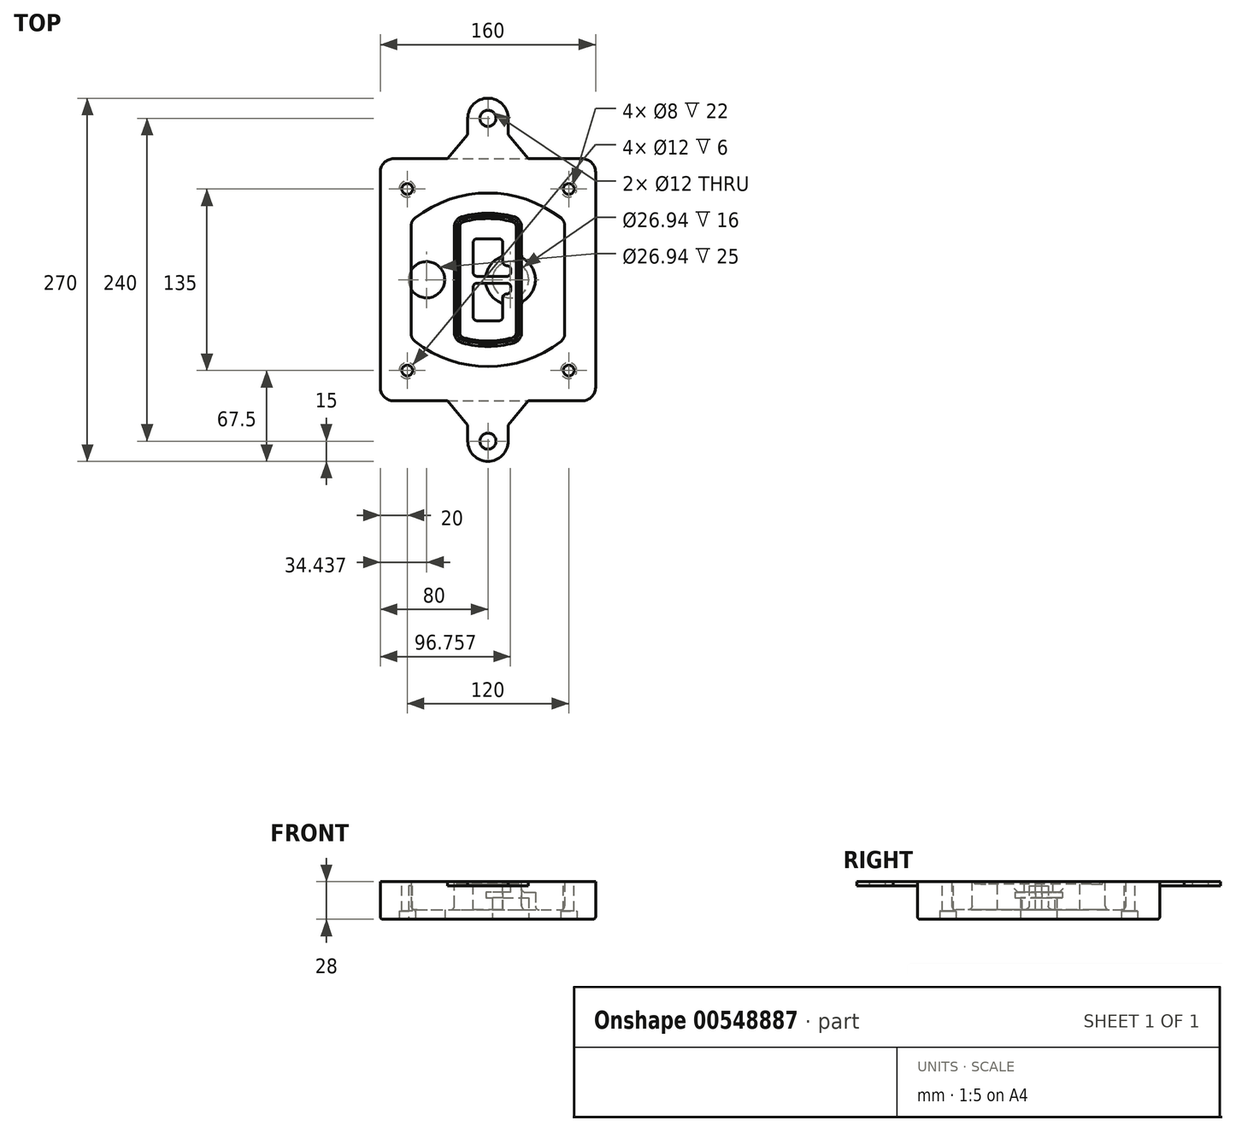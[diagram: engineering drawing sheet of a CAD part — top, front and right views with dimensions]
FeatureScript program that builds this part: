
annotation { "Feature Type Name" : "Feature", "Feature Type Description" : "" }
export const myFeature = defineFeature(function(context is Context, id is Id, definition is map)
    precondition{}
    {
        {
            var Q0;
            Q0=qCreatedBy(makeId("Top.planeOp"),FACE);
            var sketch = newSketch(context, id + "F0", { "sketchPlane" : qUnion([Q0])});
            skPoint(sketch, "E0.rect.middle", {"position": v(0, 0) * mm});
            skLineSegment(sketch, "E1.bottom", {"start": v(-70, -90) * mm, "end": v(70, -90) * mm});
            skLineSegment(sketch, "E1.top", {"start": v(-70, 90) * mm, "end": v(70, 90) * mm});
            skLineSegment(sketch, "E1.left", {"start": v(-80, -80) * mm, "end": v(-80, 80) * mm});
            skLineSegment(sketch, "E1.right", {"start": v(80, -80) * mm, "end": v(80, 80) * mm});
            skLineSegment(sketch, "E2", {"start": v(-80, 90) * mm, "end": v(80, -90) * mm, "construction": true});
            skLineSegment(sketch, "E3", {"start": v(80, 90) * mm, "end": v(-80, -90) * mm, "construction": true});
            skCircle(sketch, "E4", {"center": v(-60, 67.5) * mm, "radius": 4 * mm});
            skCircle(sketch, "E5", {"center": v(60, 67.5) * mm, "radius": 4 * mm});
            skCircle(sketch, "E6", {"center": v(60, -67.5) * mm, "radius": 4 * mm});
            skCircle(sketch, "E7", {"center": v(-60, -67.5) * mm, "radius": 4 * mm});
            skLineSegment(sketch, "E8", {"start": v(-60, 67.5) * mm, "end": v(60, 67.5) * mm, "construction": true});
            skLineSegment(sketch, "E9", {"start": v(60, 67.5) * mm, "end": v(60, -67.5) * mm, "construction": true});
            skLineSegment(sketch, "E10", {"start": v(60, -67.5) * mm, "end": v(-60, -67.5) * mm, "construction": true});
            skLineSegment(sketch, "E11", {"start": v(-60, -67.5) * mm, "end": v(-60, 67.5) * mm, "construction": true});
            skLineSegment(sketch, "E12", {"start": v(-60, 40.3) * mm, "end": v(-60, -40.3) * mm});
            skLineSegment(sketch, "E13", {"start": v(60, 40.3) * mm, "end": v(60, -40.3) * mm});
            skArc(sketch, "E14", {"start": v(56.15, 48.18) * mm, "mid": v(0, 67.5) * mm, "end": v(-56.15, 48.18) * mm});
            skArc(sketch, "E15", {"start": v(-56.15, -48.18) * mm, "mid": v(0, -67.5) * mm, "end": v(56.15, -48.18) * mm});
            skLineSegment(sketch, "E16", {"start": v(-60, 0) * mm, "end": v(60, 0) * mm, "construction": true});
            skPoint(sketch, "E17.visualSharp", {"position": v(-60, -45) * mm});
            skArc(sketch, "E17.filletArc", {"start": v(-60, -40.3) * mm, "mid": v(-58.99, -44.68) * mm, "end": v(-56.15, -48.18) * mm});
            skPoint(sketch, "E18.visualSharp", {"position": v(-60, 45) * mm});
            skArc(sketch, "E18.filletArc", {"start": v(-56.15, 48.18) * mm, "mid": v(-58.99, 44.68) * mm, "end": v(-60, 40.3) * mm});
            skPoint(sketch, "E19.visualSharp", {"position": v(60, 45) * mm});
            skArc(sketch, "E19.filletArc", {"start": v(60, 40.3) * mm, "mid": v(58.99, 44.68) * mm, "end": v(56.15, 48.18) * mm});
            skPoint(sketch, "E20.visualSharp", {"position": v(60, -45) * mm});
            skArc(sketch, "E20.filletArc", {"start": v(56.15, -48.18) * mm, "mid": v(58.99, -44.68) * mm, "end": v(60, -40.3) * mm});
            skPoint(sketch, "E21.visualSharp", {"position": v(-80, 90) * mm});
            skArc(sketch, "E21.filletArc", {"start": v(-70, 90) * mm, "mid": v(-77.07, 87.07) * mm, "end": v(-80, 80) * mm});
            skPoint(sketch, "E22.visualSharp", {"position": v(80, 90) * mm});
            skArc(sketch, "E22.filletArc", {"start": v(80, 80) * mm, "mid": v(77.07, 87.07) * mm, "end": v(70, 90) * mm});
            skPoint(sketch, "E23.visualSharp", {"position": v(80, -90) * mm});
            skArc(sketch, "E23.filletArc", {"start": v(70, -90) * mm, "mid": v(77.07, -87.07) * mm, "end": v(80, -80) * mm});
            skPoint(sketch, "E24.visualSharp", {"position": v(-80, -90) * mm});
            skArc(sketch, "E24.filletArc", {"start": v(-80, -80) * mm, "mid": v(-77.07, -87.07) * mm, "end": v(-70, -90) * mm});
            skArc(sketch, "E25.0", {"start": v(57, 40.3) * mm, "mid": v(56.3, 43.36) * mm, "end": v(54.3, 45.81) * mm});
            skLineSegment(sketch, "E25.1", {"start": v(57, 40.3) * mm, "end": v(57, -40.3) * mm});
            skArc(sketch, "E25.2", {"start": v(54.3, -45.81) * mm, "mid": v(56.3, -43.36) * mm, "end": v(57, -40.3) * mm});
            skArc(sketch, "E25.3", {"start": v(-54.3, -45.81) * mm, "mid": v(0, -64.5) * mm, "end": v(54.3, -45.81) * mm});
            skArc(sketch, "E25.4", {"start": v(-57, -40.3) * mm, "mid": v(-56.3, -43.36) * mm, "end": v(-54.3, -45.81) * mm});
            skArc(sketch, "E25.5", {"start": v(54.3, 45.81) * mm, "mid": v(0, 64.5) * mm, "end": v(-54.3, 45.81) * mm});
            skLineSegment(sketch, "E25.6", {"start": v(-57, 40.3) * mm, "end": v(-57, -40.3) * mm});
            skArc(sketch, "E25.7", {"start": v(-54.3, 45.81) * mm, "mid": v(-56.3, 43.36) * mm, "end": v(-57, 40.3) * mm});
            skArc(sketch, "E26.0", {"start": v(-58.62, 51.33) * mm, "mid": v(-62.58, 46.43) * mm, "end": v(-64, 40.3) * mm});
            skArc(sketch, "E26.1", {"start": v(58.62, 51.33) * mm, "mid": v(0, 71.5) * mm, "end": v(-58.62, 51.33) * mm});
            skArc(sketch, "E26.2", {"start": v(64, 40.3) * mm, "mid": v(62.58, 46.43) * mm, "end": v(58.62, 51.33) * mm});
            skLineSegment(sketch, "E26.3", {"start": v(64, 40.3) * mm, "end": v(64, -40.3) * mm});
            skArc(sketch, "E26.4", {"start": v(58.62, -51.33) * mm, "mid": v(62.58, -46.43) * mm, "end": v(64, -40.3) * mm});
            skLineSegment(sketch, "E26.5", {"start": v(-64, 40.3) * mm, "end": v(-64, -40.3) * mm});
            skArc(sketch, "E26.6", {"start": v(-58.62, -51.33) * mm, "mid": v(0, -71.5) * mm, "end": v(58.62, -51.33) * mm});
            skArc(sketch, "E26.7", {"start": v(-64, -40.3) * mm, "mid": v(-62.58, -46.43) * mm, "end": v(-58.62, -51.33) * mm});
            skSolve(sketch);
        }
        {
            var Q0;
            Q0=makeQuery(id+"F0.imprint","IMPRINT",FACE,{"disambiguationData":[TD([[makeQuery(id+"F0.imprint","IMPRINT",EDGE,{"derivedFrom":sQuery(id+"F0.wireOp",EDGE,"E1.bottom")}),1.0]])]});
            var Q1;
            Q1=makeQuery(id+"F0.imprint","IMPRINT",FACE,{"disambiguationData":[TD([[makeQuery(id+"F0.imprint","IMPRINT",EDGE,{"derivedFrom":sQuery(id+"F0.wireOp",EDGE,"E12")}),1.0]])]});
            var Q2;
            Q2=makeQuery(id+"F0.imprint","IMPRINT",FACE,{"disambiguationData":[TD([[makeQuery(id+"F0.imprint","IMPRINT",EDGE,{"derivedFrom":sQuery(id+"F0.wireOp",EDGE,"E25.0")}),1.0]])]});
            var Q3;
            Q3=makeQuery(id+"F0.imprint","IMPRINT",FACE,{"disambiguationData":[TD([[makeQuery(id+"F0.imprint","IMPRINT",EDGE,{"derivedFrom":sQuery(id+"F0.wireOp",EDGE,"E12")}),-1.0]])]});
            extrude(context, id + "F1", {"entities" : qUnion([Q0, Q1, Q2, Q3]), "oppositeDirection" : true, "depth" : 25 * mm, "offsetDistance" : 25 * mm});
        }
        {
            var Q0;
            Q0=makeQuery(id+"F0.imprint","IMPRINT",FACE,{"disambiguationData":[TD([[makeQuery(id+"F0.imprint","IMPRINT",EDGE,{"derivedFrom":sQuery(id+"F0.wireOp",EDGE,"E12")}),1.0]])]});
            extrude(context, id + "F2", {"entities" : qUnion([Q0]), "operationType" : NewBodyOperationType.ADD, "depth" : 3 * mm});
        }
        {
            var Q0;
            Q0=makeQuery(id+"F0.imprint","IMPRINT",FACE,{"disambiguationData":[TD([[makeQuery(id+"F0.imprint","IMPRINT",EDGE,{"derivedFrom":sQuery(id+"F0.wireOp",EDGE,"E25.0")}),1.0]])]});
            extrude(context, id + "F3", {"entities" : qUnion([Q0]), "operationType" : NewBodyOperationType.REMOVE, "oppositeDirection" : true, "depth" : 18 * mm});
        }
        {
            var Q0;
            Q0=makeQuery(id+"F2.opExtrude","CAP_FACE",FACE,{"disambiguationData":[OSD([sQuery(id+"F0.wireOp",EDGE,"E12"),sQuery(id+"F0.wireOp",EDGE,"E13"),sQuery(id+"F0.wireOp",EDGE,"E14"),sQuery(id+"F0.wireOp",EDGE,"E15"),sQuery(id+"F0.wireOp",EDGE,"E17.filletArc"),sQuery(id+"F0.wireOp",EDGE,"E18.filletArc"),sQuery(id+"F0.wireOp",EDGE,"E19.filletArc"),sQuery(id+"F0.wireOp",EDGE,"E20.filletArc"),sQuery(id+"F0.wireOp",EDGE,"E25.0"),sQuery(id+"F0.wireOp",EDGE,"E25.1"),sQuery(id+"F0.wireOp",EDGE,"E25.2"),sQuery(id+"F0.wireOp",EDGE,"E25.3"),sQuery(id+"F0.wireOp",EDGE,"E25.4"),sQuery(id+"F0.wireOp",EDGE,"E25.5"),sQuery(id+"F0.wireOp",EDGE,"E25.6"),sQuery(id+"F0.wireOp",EDGE,"E25.7")])],"isStart":false});
            var sketch = newSketch(context, id + "F4", { "sketchPlane" : qUnion([Q0])});
            skArc(sketch, "E27.0", {"start": v(-19.08, -46.97) * mm, "mid": v(0, -49.5) * mm, "end": v(19.08, -46.97) * mm});
            skArc(sketch, "E28.0", {"start": v(19.08, 46.97) * mm, "mid": v(0, 49.5) * mm, "end": v(-19.08, 46.97) * mm});
            skLineSegment(sketch, "E29", {"start": v(-25, 39.25) * mm, "end": v(-25, -39.25) * mm});
            skLineSegment(sketch, "E30", {"start": v(25, 39.25) * mm, "end": v(25, -39.25) * mm});
            skLineSegment(sketch, "E31", {"start": v(-25, 45.1) * mm, "end": v(25, 45.1) * mm, "construction": true});
            skLineSegment(sketch, "E32", {"start": v(-25, -45.1) * mm, "end": v(25, -45.1) * mm, "construction": true});
            skPoint(sketch, "E33.visualSharp", {"position": v(-25, 45.1) * mm});
            skArc(sketch, "E33.filletArc", {"start": v(-19.08, 46.97) * mm, "mid": v(-23.35, 44.11) * mm, "end": v(-25, 39.25) * mm});
            skPoint(sketch, "E34.visualSharp", {"position": v(25, 45.1) * mm});
            skArc(sketch, "E34.filletArc", {"start": v(25, 39.25) * mm, "mid": v(23.35, 44.11) * mm, "end": v(19.08, 46.97) * mm});
            skPoint(sketch, "E35.visualSharp", {"position": v(25, -45.1) * mm});
            skArc(sketch, "E35.filletArc", {"start": v(19.08, -46.97) * mm, "mid": v(23.35, -44.11) * mm, "end": v(25, -39.25) * mm});
            skPoint(sketch, "E36.visualSharp", {"position": v(-25, -45.1) * mm});
            skArc(sketch, "E36.filletArc", {"start": v(-25, -39.25) * mm, "mid": v(-23.35, -44.11) * mm, "end": v(-19.08, -46.97) * mm});
            skArc(sketch, "E37.0", {"start": v(54.3, 45.81) * mm, "mid": v(0, 64.5) * mm, "end": v(-54.3, 45.81) * mm});
            skArc(sketch, "E37.1", {"start": v(-54.3, 45.81) * mm, "mid": v(-56.3, 43.36) * mm, "end": v(-57, 40.3) * mm});
            skLineSegment(sketch, "E37.2", {"start": v(-57, 40.3) * mm, "end": v(-57, -40.3) * mm});
            skArc(sketch, "E37.3", {"start": v(-57, -40.3) * mm, "mid": v(-56.3, -43.36) * mm, "end": v(-54.3, -45.81) * mm});
            skArc(sketch, "E37.4", {"start": v(-54.3, -45.81) * mm, "mid": v(0, -64.5) * mm, "end": v(54.3, -45.81) * mm});
            skArc(sketch, "E37.5", {"start": v(54.3, -45.81) * mm, "mid": v(56.3, -43.36) * mm, "end": v(57, -40.3) * mm});
            skLineSegment(sketch, "E37.6", {"start": v(57, 40.3) * mm, "end": v(57, -40.3) * mm});
            skArc(sketch, "E37.7", {"start": v(57, 40.3) * mm, "mid": v(56.3, 43.36) * mm, "end": v(54.3, 45.81) * mm});
            skLineSegment(sketch, "E38.0", {"start": v(23, 39.25) * mm, "end": v(23, -39.25) * mm});
            skArc(sketch, "E38.1", {"start": v(18.56, -45.04) * mm, "mid": v(21.76, -42.9) * mm, "end": v(23, -39.25) * mm});
            skArc(sketch, "E38.2", {"start": v(-18.56, -45.04) * mm, "mid": v(0, -47.5) * mm, "end": v(18.56, -45.04) * mm});
            skArc(sketch, "E38.3", {"start": v(-23, -39.25) * mm, "mid": v(-21.76, -42.9) * mm, "end": v(-18.56, -45.04) * mm});
            skLineSegment(sketch, "E38.4", {"start": v(-23, 39.25) * mm, "end": v(-23, -39.25) * mm});
            skArc(sketch, "E38.5", {"start": v(23, 39.25) * mm, "mid": v(21.76, 42.9) * mm, "end": v(18.56, 45.04) * mm});
            skArc(sketch, "E38.6", {"start": v(-18.56, 45.04) * mm, "mid": v(-21.76, 42.9) * mm, "end": v(-23, 39.25) * mm});
            skArc(sketch, "E38.7", {"start": v(18.56, 45.04) * mm, "mid": v(0, 47.5) * mm, "end": v(-18.56, 45.04) * mm});
            skArc(sketch, "E39.0", {"start": v(21, 39.25) * mm, "mid": v(20.18, 41.68) * mm, "end": v(18.04, 43.1) * mm});
            skLineSegment(sketch, "E39.1", {"start": v(21, 39.25) * mm, "end": v(21, -39.25) * mm});
            skArc(sketch, "E39.2", {"start": v(18.04, -43.1) * mm, "mid": v(20.18, -41.68) * mm, "end": v(21, -39.25) * mm});
            skArc(sketch, "E39.3", {"start": v(-18.04, -43.1) * mm, "mid": v(0, -45.5) * mm, "end": v(18.04, -43.1) * mm});
            skArc(sketch, "E39.4", {"start": v(-21, -39.25) * mm, "mid": v(-20.18, -41.68) * mm, "end": v(-18.04, -43.1) * mm});
            skArc(sketch, "E39.5", {"start": v(18.04, 43.1) * mm, "mid": v(0, 45.5) * mm, "end": v(-18.04, 43.1) * mm});
            skLineSegment(sketch, "E39.6", {"start": v(-21, 39.25) * mm, "end": v(-21, -39.25) * mm});
            skArc(sketch, "E39.7", {"start": v(-18.04, 43.1) * mm, "mid": v(-20.18, 41.68) * mm, "end": v(-21, 39.25) * mm});
            skLineSegment(sketch, "E40", {"start": v(-25, 0) * mm, "end": v(25, 0) * mm, "construction": true});
            skLineSegment(sketch, "E41", {"start": v(-11, 5.5) * mm, "end": v(-11, 27.5) * mm});
            skLineSegment(sketch, "E42", {"start": v(-8, 30.5) * mm, "end": v(8, 30.5) * mm});
            skLineSegment(sketch, "E43", {"start": v(11, 27.5) * mm, "end": v(11, 13.5) * mm});
            skLineSegment(sketch, "E44", {"start": v(14, 10.5) * mm, "end": v(14, 10.5) * mm});
            skLineSegment(sketch, "E45", {"start": v(17, 7.5) * mm, "end": v(17, 5.5) * mm});
            skLineSegment(sketch, "E46", {"start": v(14, 2.5) * mm, "end": v(-8, 2.5) * mm});
            skPoint(sketch, "E47.visualSharp", {"position": v(-11, 30.5) * mm});
            skArc(sketch, "E47.filletArc", {"start": v(-8, 30.5) * mm, "mid": v(-10.12, 29.62) * mm, "end": v(-11, 27.5) * mm});
            skPoint(sketch, "E48.visualSharp", {"position": v(11, 30.5) * mm});
            skArc(sketch, "E48.filletArc", {"start": v(11, 27.5) * mm, "mid": v(10.12, 29.62) * mm, "end": v(8, 30.5) * mm});
            skPoint(sketch, "E49.visualSharp", {"position": v(11, 10.5) * mm});
            skArc(sketch, "E49.filletArc", {"start": v(11, 13.5) * mm, "mid": v(11.88, 11.38) * mm, "end": v(14, 10.5) * mm});
            skPoint(sketch, "E50.visualSharp", {"position": v(17, 10.5) * mm});
            skArc(sketch, "E50.filletArc", {"start": v(17, 7.5) * mm, "mid": v(16.12, 9.62) * mm, "end": v(14, 10.5) * mm});
            skPoint(sketch, "E51.visualSharp", {"position": v(17, 2.5) * mm});
            skArc(sketch, "E51.filletArc", {"start": v(14, 2.5) * mm, "mid": v(16.12, 3.38) * mm, "end": v(17, 5.5) * mm});
            skPoint(sketch, "E52.visualSharp", {"position": v(-11, 2.5) * mm});
            skArc(sketch, "E52.filletArc", {"start": v(-11, 5.5) * mm, "mid": v(-10.12, 3.38) * mm, "end": v(-8, 2.5) * mm});
            skLineSegment(sketch, "E53.0.MirrorCS", {"start": v(14, -2.5) * mm, "end": v(-8, -2.5) * mm});
            skArc(sketch, "E54.0.MirrorCS", {"start": v(-11, -5.5) * mm, "mid": v(-10.12, -3.38) * mm, "end": v(-8, -2.5) * mm});
            skLineSegment(sketch, "E55.0.MirrorCS", {"start": v(-11, -5.5) * mm, "end": v(-11, -27.5) * mm});
            skArc(sketch, "E56.0.MirrorCS", {"start": v(-8, -30.5) * mm, "mid": v(-10.12, -29.62) * mm, "end": v(-11, -27.5) * mm});
            skLineSegment(sketch, "E57.0.MirrorCS", {"start": v(-8, -30.5) * mm, "end": v(8, -30.5) * mm});
            skArc(sketch, "E58.0.MirrorCS", {"start": v(11, -27.5) * mm, "mid": v(10.12, -29.62) * mm, "end": v(8, -30.5) * mm});
            skLineSegment(sketch, "E59.0.MirrorCS", {"start": v(11, -27.5) * mm, "end": v(11, -13.5) * mm});
            skArc(sketch, "E60.0.MirrorCS", {"start": v(11, -13.5) * mm, "mid": v(11.88, -11.38) * mm, "end": v(14, -10.5) * mm});
            skArc(sketch, "E61.0.MirrorCS", {"start": v(17, -7.5) * mm, "mid": v(16.12, -9.62) * mm, "end": v(14, -10.5) * mm});
            skLineSegment(sketch, "E62.0.MirrorCS", {"start": v(17, -7.5) * mm, "end": v(17, -5.5) * mm});
            skArc(sketch, "E63.0.MirrorCS", {"start": v(14, -2.5) * mm, "mid": v(16.12, -3.38) * mm, "end": v(17, -5.5) * mm});
            skSolve(sketch);
        }
        {
            var Q0;
            Q0=makeQuery(id+"F4.imprint","IMPRINT",FACE,{"disambiguationData":[TD([[makeQuery(id+"F4.imprint","IMPRINT",EDGE,{"derivedFrom":sQuery(id+"F4.wireOp",EDGE,"E27.0")}),1.0]])]});
            var Q1;
            Q1=makeQuery(id+"F4.imprint","IMPRINT",FACE,{"disambiguationData":[TD([[makeQuery(id+"F4.imprint","IMPRINT",EDGE,{"derivedFrom":sQuery(id+"F4.wireOp",EDGE,"E38.0")}),-1.0]])]});
            var Q2;
            Q2=makeQuery(id+"F4.imprint","IMPRINT",FACE,{"disambiguationData":[TD([[makeQuery(id+"F4.imprint","IMPRINT",EDGE,{"derivedFrom":sQuery(id+"F4.wireOp",EDGE,"E39.0")}),1.0]])]});
            extrude(context, id + "F5", {"entities" : qUnion([Q0, Q1, Q2]), "operationType" : NewBodyOperationType.ADD, "endBound" : BoundingType.UP_TO_NEXT, "oppositeDirection" : true, "depth" : 25 * mm});
        }
        {
            var Q0;
            Q0=makeQuery(id+"F4.imprint","IMPRINT",FACE,{"disambiguationData":[TD([[makeQuery(id+"F4.imprint","IMPRINT",EDGE,{"derivedFrom":sQuery(id+"F4.wireOp",EDGE,"E38.0")}),-1.0]])]});
            extrude(context, id + "F6", {"entities" : qUnion([Q0]), "operationType" : NewBodyOperationType.REMOVE, "oppositeDirection" : true, "depth" : 2 * mm});
        }
        {
            var Q0;
            Q0=makeQuery(id+"F1.opExtrude","CAP_FACE",FACE,{"disambiguationData":[OSD([sQuery(id+"F0.wireOp",EDGE,"E1.bottom"),sQuery(id+"F0.wireOp",EDGE,"E1.top"),sQuery(id+"F0.wireOp",EDGE,"E1.left"),sQuery(id+"F0.wireOp",EDGE,"E1.right"),sQuery(id+"F0.wireOp",EDGE,"E4"),sQuery(id+"F0.wireOp",EDGE,"E5"),sQuery(id+"F0.wireOp",EDGE,"E6"),sQuery(id+"F0.wireOp",EDGE,"E7"),sQuery(id+"F0.wireOp",EDGE,"E21.filletArc"),sQuery(id+"F0.wireOp",EDGE,"E22.filletArc"),sQuery(id+"F0.wireOp",EDGE,"E23.filletArc"),sQuery(id+"F0.wireOp",EDGE,"E24.filletArc")])],"isStart":false});
            var sketch = newSketch(context, id + "F7", { "sketchPlane" : qUnion([Q0])});
            skCircle(sketch, "E64", {"center": v(16.76, 0) * mm, "radius": 13.47 * mm});
            skCircle(sketch, "E65", {"center": v(-45.56, 0) * mm, "radius": 13.47 * mm});
            skLineSegment(sketch, "E66", {"start": v(80, 0) * mm, "end": v(-80, 0) * mm});
            skCircle(sketch, "E67", {"center": v(16.76, 0) * mm, "radius": 18.47 * mm});
            skCircle(sketch, "E68", {"center": v(60, -67.5) * mm, "radius": 6 * mm});
            skCircle(sketch, "E69", {"center": v(-60, -67.5) * mm, "radius": 6 * mm});
            skCircle(sketch, "E70", {"center": v(-60, 67.5) * mm, "radius": 6 * mm});
            skCircle(sketch, "E71", {"center": v(60, 67.5) * mm, "radius": 6 * mm});
            skSolve(sketch);
        }
        {
            var Q0;
            {var subQ1=sQuery(id+"F7.wireOp",EDGE,"E66");var subQ4=sQuery(id+"F7.wireOp",EDGE,"E64");var subQ6=makeQuery(id+"F7.imprint","INTERSECT",VERTEX,{"disambiguationData":[OD(0.0)],"derivedFrom":[subQ4,subQ1]});Q0=makeQuery(id+"F7.imprint","IMPRINT",FACE,{"disambiguationData":[TD([[makeQuery(id+"F7.imprint","IMPRINT",EDGE,{"disambiguationData":[TD([[subQ6,-1.0]])],"derivedFrom":subQ4}),-1.0]])]});}
            var Q1;
            {var subQ0=sQuery(id+"F7.wireOp",EDGE,"E66");var subQ1=sQuery(id+"F7.wireOp",EDGE,"E64");var subQ3=makeQuery(id+"F7.imprint","INTERSECT",VERTEX,{"disambiguationData":[OD(0.0)],"derivedFrom":[subQ1,subQ0]});Q1=makeQuery(id+"F7.imprint","IMPRINT",FACE,{"disambiguationData":[TD([[makeQuery(id+"F7.imprint","IMPRINT",EDGE,{"disambiguationData":[TD([[subQ3,-1.0]])],"derivedFrom":subQ1}),1.0]])]});}
            var Q2;
            {var subQ0=sQuery(id+"F7.wireOp",EDGE,"E66");var subQ1=sQuery(id+"F7.wireOp",EDGE,"E64");var subQ3=makeQuery(id+"F7.imprint","INTERSECT",VERTEX,{"disambiguationData":[OD(0.0)],"derivedFrom":[subQ1,subQ0]});Q2=makeQuery(id+"F7.imprint","IMPRINT",FACE,{"disambiguationData":[TD([[makeQuery(id+"F7.imprint","IMPRINT",EDGE,{"disambiguationData":[TD([[subQ3,1.0]])],"derivedFrom":subQ1}),1.0]])]});}
            var Q3;
            {var subQ1=sQuery(id+"F7.wireOp",EDGE,"E66");var subQ4=sQuery(id+"F7.wireOp",EDGE,"E64");var subQ6=makeQuery(id+"F7.imprint","INTERSECT",VERTEX,{"disambiguationData":[OD(0.0)],"derivedFrom":[subQ4,subQ1]});Q3=makeQuery(id+"F7.imprint","IMPRINT",FACE,{"disambiguationData":[TD([[makeQuery(id+"F7.imprint","IMPRINT",EDGE,{"disambiguationData":[TD([[subQ6,1.0]])],"derivedFrom":subQ4}),-1.0]])]});}
            extrude(context, id + "F8", {"entities" : qUnion([Q0, Q1, Q2, Q3]), "operationType" : NewBodyOperationType.ADD, "oppositeDirection" : true, "depth" : 20 * mm});
        }
        {
            var Q0;
            {var subQ0=sQuery(id+"F7.wireOp",EDGE,"E66");var subQ1=sQuery(id+"F7.wireOp",EDGE,"E64");var subQ3=makeQuery(id+"F7.imprint","INTERSECT",VERTEX,{"disambiguationData":[OD(0.0)],"derivedFrom":[subQ1,subQ0]});Q0=makeQuery(id+"F7.imprint","IMPRINT",FACE,{"disambiguationData":[TD([[makeQuery(id+"F7.imprint","IMPRINT",EDGE,{"disambiguationData":[TD([[subQ3,-1.0]])],"derivedFrom":subQ1}),1.0]])]});}
            var Q1;
            {var subQ0=sQuery(id+"F7.wireOp",EDGE,"E66");var subQ1=sQuery(id+"F7.wireOp",EDGE,"E64");var subQ3=makeQuery(id+"F7.imprint","INTERSECT",VERTEX,{"disambiguationData":[OD(0.0)],"derivedFrom":[subQ1,subQ0]});Q1=makeQuery(id+"F7.imprint","IMPRINT",FACE,{"disambiguationData":[TD([[makeQuery(id+"F7.imprint","IMPRINT",EDGE,{"disambiguationData":[TD([[subQ3,1.0]])],"derivedFrom":subQ1}),1.0]])]});}
            extrude(context, id + "F9", {"entities" : qUnion([Q0, Q1]), "operationType" : NewBodyOperationType.REMOVE, "oppositeDirection" : true, "depth" : 16 * mm});
        }
        {
            var Q0;
            {var subQ0=sQuery(id+"F7.wireOp",EDGE,"E66");var subQ1=sQuery(id+"F7.wireOp",EDGE,"E65");var subQ3=makeQuery(id+"F7.imprint","INTERSECT",VERTEX,{"disambiguationData":[OD(0.0)],"derivedFrom":[subQ1,subQ0]});Q0=makeQuery(id+"F7.imprint","IMPRINT",FACE,{"disambiguationData":[TD([[makeQuery(id+"F7.imprint","IMPRINT",EDGE,{"disambiguationData":[TD([[subQ3,-1.0]])],"derivedFrom":subQ1}),1.0]])]});}
            var Q1;
            {var subQ0=sQuery(id+"F7.wireOp",EDGE,"E66");var subQ1=sQuery(id+"F7.wireOp",EDGE,"E65");var subQ3=makeQuery(id+"F7.imprint","INTERSECT",VERTEX,{"disambiguationData":[OD(0.0)],"derivedFrom":[subQ1,subQ0]});Q1=makeQuery(id+"F7.imprint","IMPRINT",FACE,{"disambiguationData":[TD([[makeQuery(id+"F7.imprint","IMPRINT",EDGE,{"disambiguationData":[TD([[subQ3,1.0]])],"derivedFrom":subQ1}),1.0]])]});}
            extrude(context, id + "F10", {"entities" : qUnion([Q0, Q1]), "operationType" : NewBodyOperationType.REMOVE, "oppositeDirection" : true, "depth" : 25 * mm});
        }
        {
            var Q0;
            Q0=makeQuery(id+"F7.imprint","IMPRINT",FACE,{"disambiguationData":[TD([[makeQuery(id+"F7.imprint","IMPRINT",EDGE,{"derivedFrom":sQuery(id+"F7.wireOp",EDGE,"E68")}),1.0]])]});
            var Q1;
            Q1=makeQuery(id+"F7.imprint","IMPRINT",FACE,{"disambiguationData":[TD([[makeQuery(id+"F7.imprint","IMPRINT",EDGE,{"derivedFrom":makeQuery(id+"F1.opExtrude","CAP_EDGE",EDGE,{"disambiguationData":[OSD([sQuery(id+"F0.wireOp",EDGE,"E5")])],"isStart":false})}),-1.0]])]});
            var Q2;
            Q2=makeQuery(id+"F7.imprint","IMPRINT",FACE,{"disambiguationData":[TD([[makeQuery(id+"F7.imprint","IMPRINT",EDGE,{"derivedFrom":sQuery(id+"F7.wireOp",EDGE,"E69")}),1.0]])]});
            var Q3;
            Q3=makeQuery(id+"F7.imprint","IMPRINT",FACE,{"disambiguationData":[TD([[makeQuery(id+"F7.imprint","IMPRINT",EDGE,{"derivedFrom":makeQuery(id+"F1.opExtrude","CAP_EDGE",EDGE,{"disambiguationData":[OSD([sQuery(id+"F0.wireOp",EDGE,"E4")])],"isStart":false})}),-1.0]])]});
            var Q4;
            Q4=makeQuery(id+"F7.imprint","IMPRINT",FACE,{"disambiguationData":[TD([[makeQuery(id+"F7.imprint","IMPRINT",EDGE,{"derivedFrom":sQuery(id+"F7.wireOp",EDGE,"E70")}),1.0]])]});
            var Q5;
            Q5=makeQuery(id+"F7.imprint","IMPRINT",FACE,{"disambiguationData":[TD([[makeQuery(id+"F7.imprint","IMPRINT",EDGE,{"derivedFrom":makeQuery(id+"F1.opExtrude","CAP_EDGE",EDGE,{"disambiguationData":[OSD([sQuery(id+"F0.wireOp",EDGE,"E7")])],"isStart":false})}),-1.0]])]});
            var Q6;
            Q6=makeQuery(id+"F7.imprint","IMPRINT",FACE,{"disambiguationData":[TD([[makeQuery(id+"F7.imprint","IMPRINT",EDGE,{"derivedFrom":sQuery(id+"F7.wireOp",EDGE,"E71")}),1.0]])]});
            var Q7;
            Q7=makeQuery(id+"F7.imprint","IMPRINT",FACE,{"disambiguationData":[TD([[makeQuery(id+"F7.imprint","IMPRINT",EDGE,{"derivedFrom":makeQuery(id+"F1.opExtrude","CAP_EDGE",EDGE,{"disambiguationData":[OSD([sQuery(id+"F0.wireOp",EDGE,"E6")])],"isStart":false})}),-1.0]])]});
            extrude(context, id + "F11", {"entities" : qUnion([Q0, Q1, Q2, Q3, Q4, Q5, Q6, Q7]), "operationType" : NewBodyOperationType.REMOVE, "oppositeDirection" : true, "depth" : 6 * mm});
        }
        {
            var Q0;
            Q0=makeQuery(id+"F9.boolean.opBoolean","COPY",FACE,{"derivedFrom":makeQuery(id+"F9.opExtrude","CAP_FACE",FACE,{"disambiguationData":[OSD([sQuery(id+"F7.wireOp",EDGE,"E64")])],"isStart":false})});
            var sketch = newSketch(context, id + "F12", { "sketchPlane" : qUnion([Q0])});
            skArc(sketch, "E72.0", {"start": v(11, 17.55) * mm, "mid": v(2.57, 11.82) * mm, "end": v(-1.54, 2.5) * mm});
            skArc(sketch, "E72.1", {"start": v(-1.54, -2.5) * mm, "mid": v(2.57, -11.82) * mm, "end": v(11, -17.55) * mm});
            skLineSegment(sketch, "E73", {"start": v(-1.54, -2.5) * mm, "end": v(14, -2.5) * mm});
            skLineSegment(sketch, "E74.0", {"start": v(14, 2.5) * mm, "end": v(-1.54, 2.5) * mm});
            skArc(sketch, "E74.1", {"start": v(14, 2.5) * mm, "mid": v(16.12, 3.38) * mm, "end": v(17, 5.5) * mm});
            skLineSegment(sketch, "E74.2", {"start": v(17, 7.5) * mm, "end": v(17, 5.5) * mm});
            skArc(sketch, "E74.3", {"start": v(17, 7.5) * mm, "mid": v(16.12, 9.62) * mm, "end": v(14, 10.5) * mm});
            skArc(sketch, "E74.4", {"start": v(11, 13.5) * mm, "mid": v(11.88, 11.38) * mm, "end": v(14, 10.5) * mm});
            skLineSegment(sketch, "E74.5", {"start": v(11, 17.55) * mm, "end": v(11, 13.5) * mm});
            skLineSegment(sketch, "E74.7", {"start": v(14, -2.5) * mm, "end": v(-1.54, -2.5) * mm});
            skArc(sketch, "E74.8", {"start": v(14, -2.5) * mm, "mid": v(16.12, -3.38) * mm, "end": v(17, -5.5) * mm});
            skLineSegment(sketch, "E74.9", {"start": v(17, -7.5) * mm, "end": v(17, -5.5) * mm});
            skArc(sketch, "E74.10", {"start": v(17, -7.5) * mm, "mid": v(16.12, -9.62) * mm, "end": v(14, -10.5) * mm});
            skArc(sketch, "E74.11", {"start": v(11, -13.5) * mm, "mid": v(11.88, -11.38) * mm, "end": v(14, -10.5) * mm});
            skLineSegment(sketch, "E74.12", {"start": v(11, -17.55) * mm, "end": v(11, -13.5) * mm});
            skPoint(sketch, "E75.orphan", {"position": v(11, -27.5) * mm});
            skPoint(sketch, "E76.orphan", {"position": v(-8, -2.5) * mm});
            skPoint(sketch, "E77.orphan", {"position": v(-8, 2.5) * mm});
            skPoint(sketch, "E78.orphan", {"position": v(11, 27.5) * mm});
            skSolve(sketch);
        }
        {
            var Q0;
            {var subQ7=sQuery(id+"F12.wireOp",EDGE,"E72.0");var subQ14=sQuery(id+"F12.wireOp",EDGE,"E72.1");var subQ16=sQuery(id+"F12.wireOp",EDGE,"E74.1");var subQ18=sQuery(id+"F12.wireOp",EDGE,"E74.8");Q0=qUnion([makeQuery(id+"F12.imprint","IMPRINT",FACE,{"disambiguationData":[TD([[makeQuery(id+"F12.imprint","IMPRINT",EDGE,{"derivedFrom":subQ7}),1.0]])]}),makeQuery(id+"F12.imprint","IMPRINT",FACE,{"disambiguationData":[TD([[makeQuery(id+"F12.imprint","IMPRINT",EDGE,{"derivedFrom":subQ14}),1.0]])]}),makeQuery(id+"F12.imprint","IMPRINT",FACE,{"disambiguationData":[TD([[makeQuery(id+"F12.imprint","IMPRINT",EDGE,{"derivedFrom":subQ16}),1.0]])]}),makeQuery(id+"F12.imprint","IMPRINT",FACE,{"disambiguationData":[TD([[makeQuery(id+"F12.imprint","IMPRINT",EDGE,{"derivedFrom":subQ18}),-1.0]])]})]);}
            var Q1;
            Q1=makeQuery(id+"F5.boolean.opBoolean","SPLIT",FACE,{"disambiguationData":[TD([makeQuery(id+"F5.opExtrude","SWEPT_FACE",FACE,{"disambiguationData":[OSD([sQuery(id+"F4.wireOp",EDGE,"E41")])]})])],"derivedFrom":makeQuery(id+"F3.boolean.opBoolean","COPY",FACE,{"derivedFrom":makeQuery(id+"F3.opExtrude","CAP_FACE",FACE,{"disambiguationData":[OSD([sQuery(id+"F0.wireOp",EDGE,"E25.0"),sQuery(id+"F0.wireOp",EDGE,"E25.1"),sQuery(id+"F0.wireOp",EDGE,"E25.2"),sQuery(id+"F0.wireOp",EDGE,"E25.3"),sQuery(id+"F0.wireOp",EDGE,"E25.4"),sQuery(id+"F0.wireOp",EDGE,"E25.5"),sQuery(id+"F0.wireOp",EDGE,"E25.6"),sQuery(id+"F0.wireOp",EDGE,"E25.7")])],"isStart":false})})});
            extrude(context, id + "F13", {"entities" : qUnion([Q0]), "operationType" : NewBodyOperationType.REMOVE, "endBound" : BoundingType.UP_TO_SURFACE, "endBoundEntityFace" : qUnion([Q1]), "depth" : 25 * mm});
        }
        {
            var Q0;
            Q0=makeQuery(id+"F3.boolean.opBoolean","COPY",EDGE,{"derivedFrom":makeQuery(id+"F3.opExtrude","CAP_EDGE",EDGE,{"disambiguationData":[OSD([sQuery(id+"F0.wireOp",EDGE,"E25.6")])],"isStart":false})});
            var Q1;
            Q1=makeQuery(id+"F8.boolean.opBoolean","INTERSECT",EDGE,{"derivedFrom":[makeQuery(id+"F5.opExtrude","SWEPT_FACE",FACE,{"disambiguationData":[OSD([sQuery(id+"F4.wireOp",EDGE,"E30")])]}),makeQuery(id+"F8.opExtrude","CAP_FACE",FACE,{"disambiguationData":[OSD([sQuery(id+"F7.wireOp",EDGE,"E67")])],"isStart":false})]});
            var Q2;
            Q2=makeQuery(id+"F8.boolean.opBoolean","INTERSECT",EDGE,{"disambiguationData":[OD(1.0)],"derivedFrom":[makeQuery(id+"F5.opExtrude","SWEPT_FACE",FACE,{"disambiguationData":[OSD([sQuery(id+"F4.wireOp",EDGE,"E30")])]}),makeQuery(id+"F8.opExtrude","SWEPT_FACE",FACE,{"disambiguationData":[OSD([sQuery(id+"F7.wireOp",EDGE,"E67")])]})]});
            var Q3;
            {var subQ0=sQuery(id+"F4.wireOp",EDGE,"E30");Q3=makeQuery(id+"F8.boolean.opBoolean","SPLIT",EDGE,{"disambiguationData":[TD([makeQuery(id+"F5.opExtrude","SWEPT_FACE",FACE,{"disambiguationData":[OSD([sQuery(id+"F4.wireOp",EDGE,"E35.filletArc")])]})])],"derivedFrom":makeQuery(id+"F5.opExtrude","CAP_EDGE",EDGE,{"disambiguationData":[OSD([subQ0])],"isStart":false})});}
            var Q4;
            {var subQ0=sQuery(id+"F0.wireOp",EDGE,"E25.7");var subQ1=sQuery(id+"F0.wireOp",EDGE,"E25.1");var subQ2=sQuery(id+"F0.wireOp",EDGE,"E25.6");var subQ3=sQuery(id+"F0.wireOp",EDGE,"E25.5");var subQ4=sQuery(id+"F0.wireOp",EDGE,"E25.4");var subQ5=sQuery(id+"F0.wireOp",EDGE,"E25.0");var subQ6=sQuery(id+"F0.wireOp",EDGE,"E25.2");var subQ7=sQuery(id+"F0.wireOp",EDGE,"E25.3");Q4=makeQuery(id+"F8.boolean.opBoolean","INTERSECT",EDGE,{"derivedFrom":[makeQuery(id+"F5.boolean.opBoolean","SPLIT",FACE,{"disambiguationData":[TD([makeQuery(id+"F2.opExtrude","SWEPT_FACE",FACE,{"disambiguationData":[OSD([subQ5])]})])],"derivedFrom":makeQuery(id+"F3.boolean.opBoolean","COPY",FACE,{"derivedFrom":makeQuery(id+"F3.opExtrude","CAP_FACE",FACE,{"disambiguationData":[OSD([subQ5,subQ1,subQ6,subQ7,subQ4,subQ3,subQ2,subQ0])],"isStart":false})})}),makeQuery(id+"F8.opExtrude","SWEPT_FACE",FACE,{"disambiguationData":[OSD([sQuery(id+"F7.wireOp",EDGE,"E67")])]})]});}
            var Q5;
            Q5=makeQuery(id+"F8.boolean.opBoolean","INTERSECT",EDGE,{"disambiguationData":[OD(0.0)],"derivedFrom":[makeQuery(id+"F5.opExtrude","SWEPT_FACE",FACE,{"disambiguationData":[OSD([sQuery(id+"F4.wireOp",EDGE,"E30")])]}),makeQuery(id+"F8.opExtrude","SWEPT_FACE",FACE,{"disambiguationData":[OSD([sQuery(id+"F7.wireOp",EDGE,"E67")])]})]});
            fillet(context, id + "F14", {"entities" : qUnion([Q0, Q1, Q2, Q3, Q4, Q5]), "radius" : 3 * mm, "tangentPropagation" : true, "allowEdgeOverflow" : false});
        }
        {
            var Q0;
            Q0=makeQuery(id+"F1.opExtrude","CAP_EDGE",EDGE,{"disambiguationData":[OSD([sQuery(id+"F0.wireOp",EDGE,"E1.bottom")])],"isStart":false});
            fillet(context, id + "F15", {"entities" : qUnion([Q0]), "radius" : 2 * mm, "tangentPropagation" : true, "allowEdgeOverflow" : false});
        }
        {
            var Q0;
            {var subQ0=sQuery(id+"F0.wireOp",EDGE,"E21.filletArc");var subQ1=sQuery(id+"F0.wireOp",EDGE,"E7");var subQ2=sQuery(id+"F0.wireOp",EDGE,"E6");var subQ3=sQuery(id+"F0.wireOp",EDGE,"E5");var subQ4=sQuery(id+"F0.wireOp",EDGE,"E4");var subQ5=sQuery(id+"F0.wireOp",EDGE,"E22.filletArc");var subQ6=sQuery(id+"F0.wireOp",EDGE,"E1.bottom");var subQ7=sQuery(id+"F0.wireOp",EDGE,"E1.right");var subQ8=sQuery(id+"F0.wireOp",EDGE,"E1.top");var subQ9=sQuery(id+"F0.wireOp",EDGE,"E1.left");var subQ10=sQuery(id+"F0.wireOp",EDGE,"E23.filletArc");var subQ11=sQuery(id+"F0.wireOp",EDGE,"E24.filletArc");Q0=makeQuery(id+"F2.boolean.opBoolean","SPLIT",FACE,{"disambiguationData":[TD([makeQuery(id+"F1.opExtrude","SWEPT_FACE",FACE,{"disambiguationData":[OSD([subQ6])]})])],"derivedFrom":makeQuery(id+"F1.opExtrude","CAP_FACE",FACE,{"disambiguationData":[OSD([subQ6,subQ8,subQ9,subQ7,subQ4,subQ3,subQ2,subQ1,subQ0,subQ5,subQ10,subQ11])],"isStart":true})});}
            var sketch = newSketch(context, id + "F16", { "sketchPlane" : qUnion([Q0])});
            skLineSegment(sketch, "E79", {"start": v(0, 90) * mm, "end": v(0, 120) * mm, "construction": true});
            skCircle(sketch, "E80", {"center": v(0, 120) * mm, "radius": 6 * mm});
            skLineSegment(sketch, "E81", {"start": v(15, 108) * mm, "end": v(15, 120) * mm});
            skArc(sketch, "E82", {"start": v(15, 120) * mm, "mid": v(0, 135) * mm, "end": v(-15, 120) * mm});
            skLineSegment(sketch, "E83", {"start": v(-80, 0) * mm, "end": v(80, 0) * mm, "construction": true});
            skLineSegment(sketch, "E84", {"start": v(-15, 120) * mm, "end": v(-15, 108) * mm});
            skLineSegment(sketch, "E85", {"start": v(15, 108) * mm, "end": v(30, 90) * mm});
            skLineSegment(sketch, "E86", {"start": v(-15, 108) * mm, "end": v(-30, 90) * mm});
            skLineSegment(sketch, "E87.MirrorCS", {"start": v(-15, -108) * mm, "end": v(-30, -90) * mm});
            skLineSegment(sketch, "E88.MirrorCS", {"start": v(-15, -120) * mm, "end": v(-15, -108) * mm});
            skArc(sketch, "E89.MirrorCS", {"start": v(15, -120) * mm, "mid": v(0, -135) * mm, "end": v(-15, -120) * mm});
            skLineSegment(sketch, "E90.MirrorCS", {"start": v(15, -108) * mm, "end": v(15, -120) * mm});
            skLineSegment(sketch, "E91.MirrorCS", {"start": v(15, -108) * mm, "end": v(30, -90) * mm});
            skLineSegment(sketch, "E92.MirrorCS", {"start": v(0, -90) * mm, "end": v(0, -120) * mm, "construction": true});
            skCircle(sketch, "E93.MirrorC", {"center": v(0, -120) * mm, "radius": 6 * mm});
            skSolve(sketch);
        }
        {
            var Q0;
            {var subQ0=sQuery(id+"F16.wireOp",EDGE,"E87.MirrorCS");Q0=makeQuery(id+"F16.imprint","IMPRINT",FACE,{"disambiguationData":[TD([[makeQuery(id+"F16.imprint","IMPRINT",EDGE,{"derivedFrom":subQ0}),-1.0]])]});}
            var Q1;
            Q1=makeQuery(id+"F16.imprint","IMPRINT",FACE,{"disambiguationData":[TD([[makeQuery(id+"F16.imprint","IMPRINT",EDGE,{"derivedFrom":sQuery(id+"F16.wireOp",EDGE,"E80")}),-1.0]])]});
            var Q2;
            Q2=makeQuery(id+"F16.imprint","IMPRINT",FACE,{"disambiguationData":[TD([[makeQuery(id+"F16.imprint","IMPRINT",EDGE,{"derivedFrom":makeQuery(id+"F1.opExtrude","CAP_EDGE",EDGE,{"disambiguationData":[OSD([sQuery(id+"F0.wireOp",EDGE,"E1.left")])],"isStart":true})}),-1.0]])]});
            var Q3;
            Q3=makeQuery(id+"F2.opExtrude","CAP_FACE",FACE,{"disambiguationData":[OSD([sQuery(id+"F0.wireOp",EDGE,"E12"),sQuery(id+"F0.wireOp",EDGE,"E13"),sQuery(id+"F0.wireOp",EDGE,"E14"),sQuery(id+"F0.wireOp",EDGE,"E15"),sQuery(id+"F0.wireOp",EDGE,"E17.filletArc"),sQuery(id+"F0.wireOp",EDGE,"E18.filletArc"),sQuery(id+"F0.wireOp",EDGE,"E19.filletArc"),sQuery(id+"F0.wireOp",EDGE,"E20.filletArc"),sQuery(id+"F0.wireOp",EDGE,"E25.0"),sQuery(id+"F0.wireOp",EDGE,"E25.1"),sQuery(id+"F0.wireOp",EDGE,"E25.2"),sQuery(id+"F0.wireOp",EDGE,"E25.3"),sQuery(id+"F0.wireOp",EDGE,"E25.4"),sQuery(id+"F0.wireOp",EDGE,"E25.5"),sQuery(id+"F0.wireOp",EDGE,"E25.6"),sQuery(id+"F0.wireOp",EDGE,"E25.7")])],"isStart":false});
            extrude(context, id + "F17", {"entities" : qUnion([Q0, Q1, Q2]), "operationType" : NewBodyOperationType.ADD, "endBound" : BoundingType.UP_TO_SURFACE, "depth" : 25 * mm, "endBoundEntityFace" : qUnion([Q3]), "offsetDistance" : 25 * mm});
        }
    });
